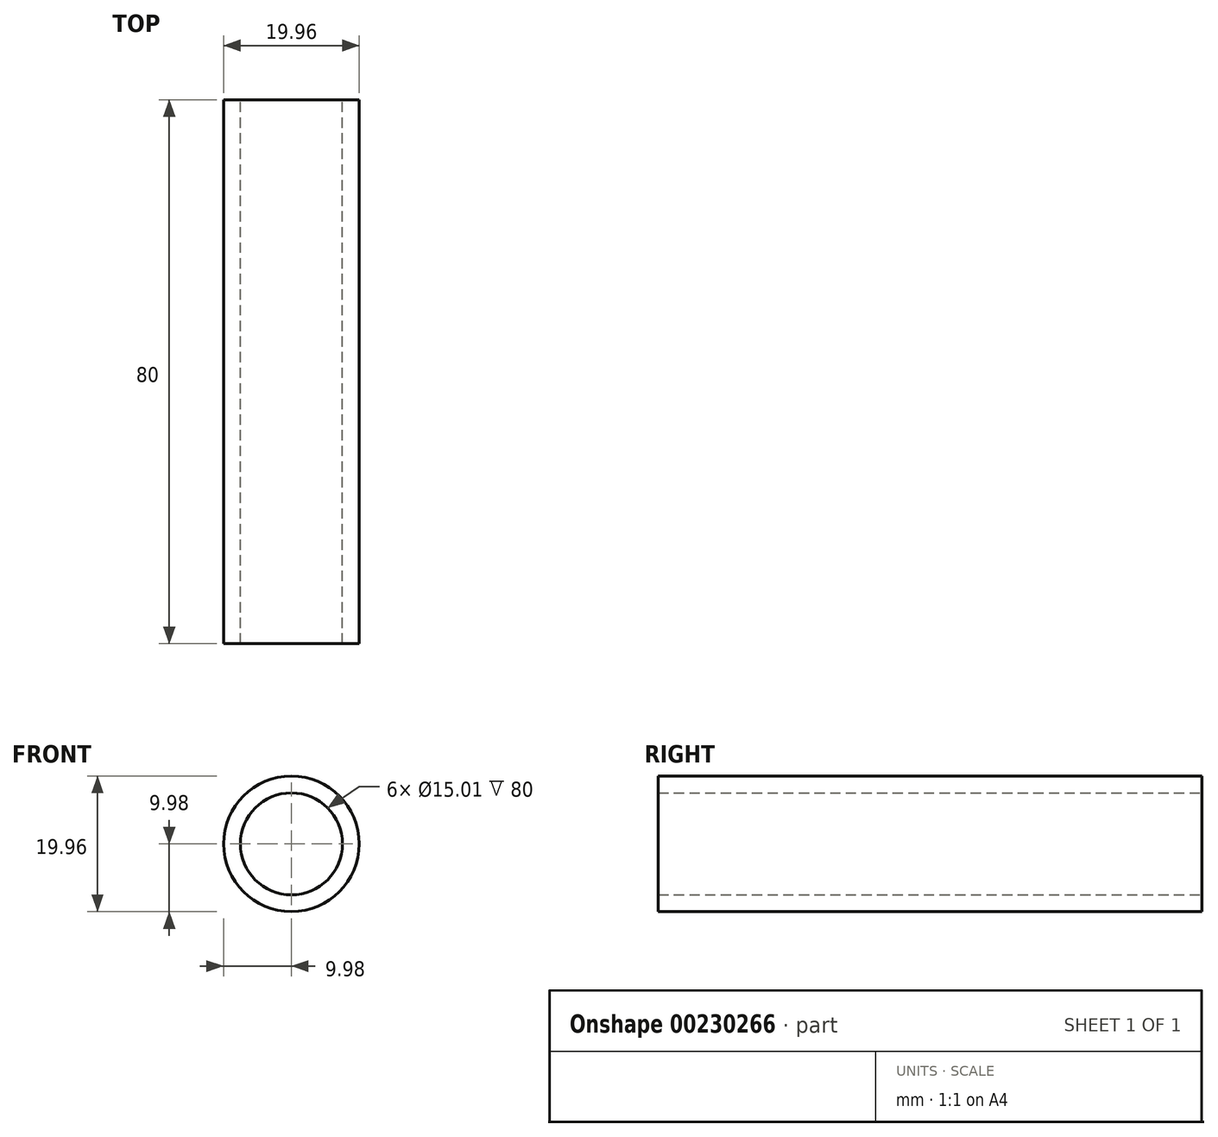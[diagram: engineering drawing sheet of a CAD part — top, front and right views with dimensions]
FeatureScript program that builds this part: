
annotation { "Feature Type Name" : "Feature", "Feature Type Description" : "" }
export const myFeature = defineFeature(function(context is Context, id is Id, definition is map)
    precondition{}
    {
        {
            var Q0;
            Q0=qCreatedBy(makeId("Front.planeOp"),FACE);
            var sketch = newSketch(context, id + "F0", { "sketchPlane" : qUnion([Q0])});
            skCircle(sketch, "E0", {"center": v(0, 0) * mm, "radius": 9.97 * mm});
            skCircle(sketch, "E1", {"center": v(0, 0) * mm, "radius": 7.5 * mm});
            skSolve(sketch);
        }
        {
            var Q0;
            Q0=makeQuery(id+"F0.imprint","IMPRINT",FACE,{"disambiguationData":[TD([[makeQuery(id+"F0.imprint","IMPRINT",EDGE,{"derivedFrom":sQuery(id+"F0.wireOp",EDGE,"E0")}),1.0]])]});
            extrude(context, id + "F1", {"entities" : qUnion([Q0]), "endBound" : BoundingType.SYMMETRIC, "depth" : 80 * mm});
        }
    });
